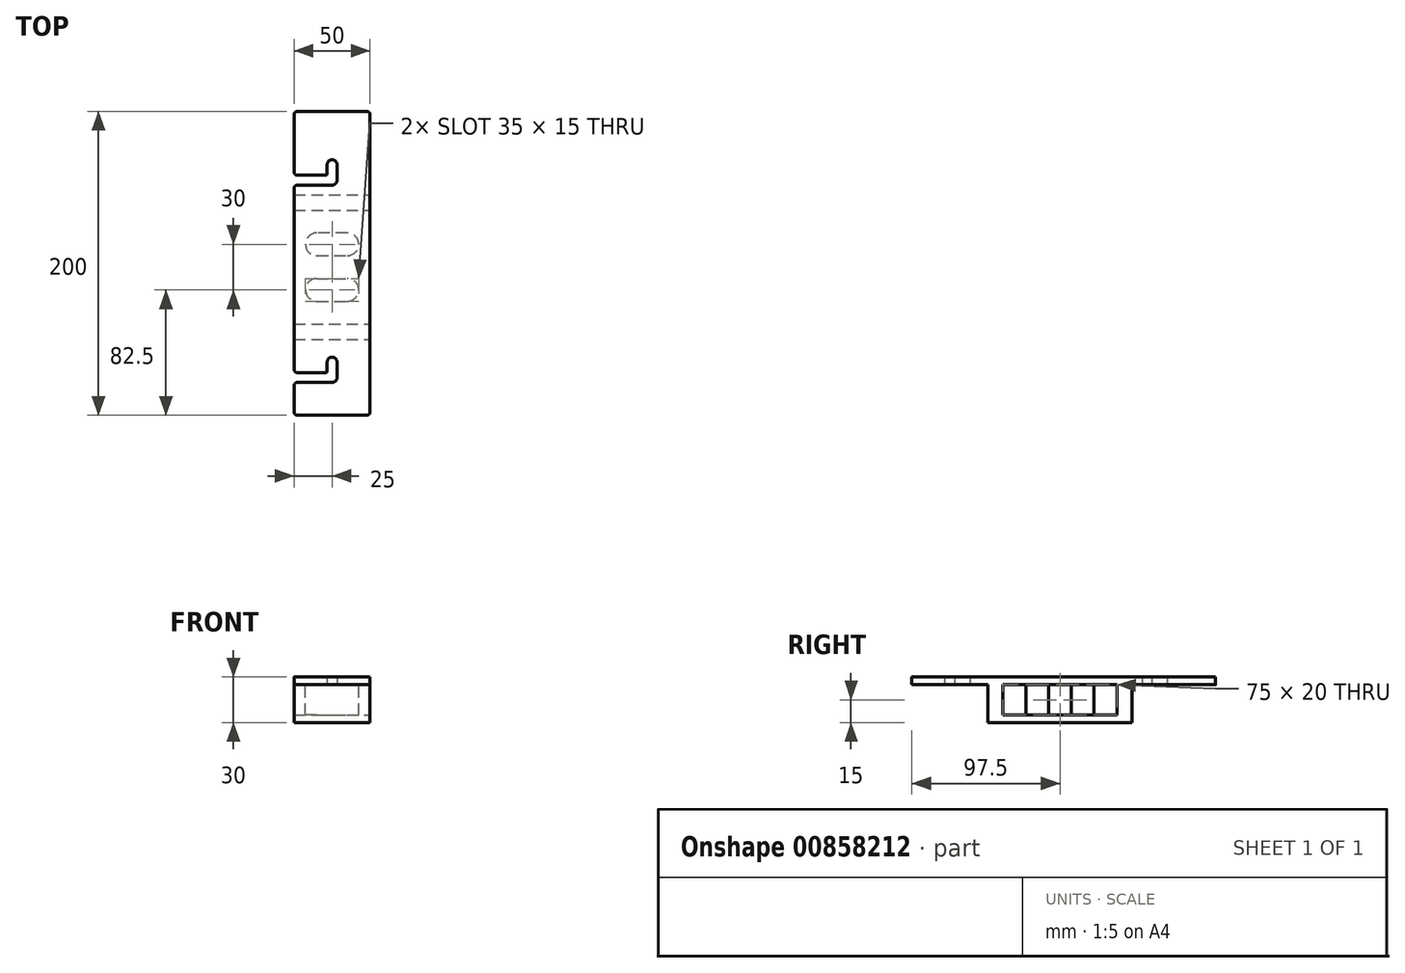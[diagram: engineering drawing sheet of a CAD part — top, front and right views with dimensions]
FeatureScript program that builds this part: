
annotation { "Feature Type Name" : "Feature", "Feature Type Description" : "" }
export const myFeature = defineFeature(function(context is Context, id is Id, definition is map)
    precondition{}
    {
        {
            var Q0;
            Q0=qCreatedBy(makeId("Top.planeOp"),FACE);
            var sketch = newSketch(context, id + "F0", { "sketchPlane" : qUnion([Q0])});
            skLineSegment(sketch, "E0.bottom", {"start": v(23, -100) * mm, "end": v(-23, -100) * mm});
            skLineSegment(sketch, "E0.top", {"start": v(23, 100) * mm, "end": v(-23, 100) * mm});
            skLineSegment(sketch, "E0.left", {"start": v(25, -98) * mm, "end": v(25, 98) * mm});
            skLineSegment(sketch, "E0.right", {"start": v(-25, -98) * mm, "end": v(-25, -80.5) * mm});
            skPoint(sketch, "E0.middle", {"position": v(0, 0) * mm});
            skLineSegment(sketch, "E1", {"start": v(-3.25, 65) * mm, "end": v(-3.25, 59) * mm});
            skLineSegment(sketch, "E2", {"start": v(-4.25, 58) * mm, "end": v(-23, 58) * mm});
            skLineSegment(sketch, "E3", {"start": v(-23, 51.5) * mm, "end": v(0, 51.5) * mm});
            skLineSegment(sketch, "E4", {"start": v(3.25, 54.75) * mm, "end": v(3.25, 65) * mm});
            skArc(sketch, "E5", {"start": v(-3.25, 65) * mm, "mid": v(0, 68.25) * mm, "end": v(3.25, 65) * mm});
            skPoint(sketch, "E6.visualSharp", {"position": v(3.25, 51.5) * mm});
            skArc(sketch, "E6.filletArc", {"start": v(0, 51.5) * mm, "mid": v(2.3, 52.45) * mm, "end": v(3.25, 54.75) * mm});
            skPoint(sketch, "E7.visualSharp", {"position": v(-3.25, 58) * mm});
            skArc(sketch, "E7.filletArc", {"start": v(-4.25, 58) * mm, "mid": v(-3.54, 58.3) * mm, "end": v(-3.25, 59) * mm});
            skLineSegment(sketch, "E8.trimOffspring", {"start": v(-25, 60) * mm, "end": v(-25, 98) * mm});
            skPoint(sketch, "E9.visualSharp", {"position": v(-25, 58) * mm});
            skArc(sketch, "E9.filletArc", {"start": v(-25, 60) * mm, "mid": v(-24.41, 58.59) * mm, "end": v(-23, 58) * mm});
            skPoint(sketch, "E10.visualSharp", {"position": v(-25, 51.5) * mm});
            skArc(sketch, "E10.filletArc", {"start": v(-23, 51.5) * mm, "mid": v(-24.41, 50.91) * mm, "end": v(-25, 49.5) * mm});
            skLineSegment(sketch, "E11", {"start": v(-3.25, -65) * mm, "end": v(-3.25, -71) * mm});
            skLineSegment(sketch, "E12", {"start": v(-4.25, -72) * mm, "end": v(-23, -72) * mm});
            skLineSegment(sketch, "E13", {"start": v(-23, -78.5) * mm, "end": v(0, -78.5) * mm});
            skLineSegment(sketch, "E14", {"start": v(3.25, -75.25) * mm, "end": v(3.25, -65) * mm});
            skArc(sketch, "E15", {"start": v(-3.25, -65) * mm, "mid": v(0, -61.75) * mm, "end": v(3.25, -65) * mm});
            skPoint(sketch, "E16.visualSharp", {"position": v(3.25, -78.5) * mm});
            skArc(sketch, "E16.filletArc", {"start": v(0, -78.5) * mm, "mid": v(2.3, -77.55) * mm, "end": v(3.25, -75.25) * mm});
            skPoint(sketch, "E17.visualSharp", {"position": v(-3.25, -72) * mm});
            skArc(sketch, "E17.filletArc", {"start": v(-4.25, -72) * mm, "mid": v(-3.54, -71.7) * mm, "end": v(-3.25, -71) * mm});
            skPoint(sketch, "E18.visualSharp", {"position": v(-24.01, -72) * mm});
            skArc(sketch, "E18.filletArc", {"start": v(-25, -70) * mm, "mid": v(-24.41, -71.41) * mm, "end": v(-23, -72) * mm});
            skPoint(sketch, "E19.visualSharp", {"position": v(-24.01, -78.5) * mm});
            skArc(sketch, "E19.filletArc", {"start": v(-23, -78.5) * mm, "mid": v(-24.41, -79.09) * mm, "end": v(-25, -80.5) * mm});
            skLineSegment(sketch, "E20.trimOffspring", {"start": v(-25, -70) * mm, "end": v(-25, 49.5) * mm});
            skPoint(sketch, "E21.visualSharp", {"position": v(-25, 100) * mm});
            skArc(sketch, "E21.filletArc", {"start": v(-23, 100) * mm, "mid": v(-24.41, 99.41) * mm, "end": v(-25, 98) * mm});
            skPoint(sketch, "E22.visualSharp", {"position": v(25, 100) * mm});
            skArc(sketch, "E22.filletArc", {"start": v(25, 98) * mm, "mid": v(24.41, 99.41) * mm, "end": v(23, 100) * mm});
            skPoint(sketch, "E23.visualSharp", {"position": v(25, -100) * mm});
            skArc(sketch, "E23.filletArc", {"start": v(23, -100) * mm, "mid": v(24.41, -99.41) * mm, "end": v(25, -98) * mm});
            skPoint(sketch, "E24.visualSharp", {"position": v(-25, -100) * mm});
            skArc(sketch, "E24.filletArc", {"start": v(-25, -98) * mm, "mid": v(-24.41, -99.41) * mm, "end": v(-23, -100) * mm});
            skSolve(sketch);
        }
        {
            var Q0;
            Q0 = qSketchRegion(id + "F0", true);
            extrude(context, id + "F1", {"entities" : qUnion([Q0]), "depth" : 5 * mm, "offsetDistance" : 25 * mm});
        }
        {
            var Q0;
            Q0=makeQuery(id+"F1.opExtrude","CAP_FACE",FACE,{"disambiguationData":[OSD([sQuery(id+"F0.wireOp",EDGE,"E0.bottom"),sQuery(id+"F0.wireOp",EDGE,"E0.top"),sQuery(id+"F0.wireOp",EDGE,"E0.left"),sQuery(id+"F0.wireOp",EDGE,"E0.right"),sQuery(id+"F0.wireOp",EDGE,"E1"),sQuery(id+"F0.wireOp",EDGE,"E2"),sQuery(id+"F0.wireOp",EDGE,"E3"),sQuery(id+"F0.wireOp",EDGE,"E4"),sQuery(id+"F0.wireOp",EDGE,"E5"),sQuery(id+"F0.wireOp",EDGE,"E6.filletArc"),sQuery(id+"F0.wireOp",EDGE,"E7.filletArc"),sQuery(id+"F0.wireOp",EDGE,"E8.trimOffspring"),sQuery(id+"F0.wireOp",EDGE,"E9.filletArc"),sQuery(id+"F0.wireOp",EDGE,"E10.filletArc"),sQuery(id+"F0.wireOp",EDGE,"E11"),sQuery(id+"F0.wireOp",EDGE,"E12"),sQuery(id+"F0.wireOp",EDGE,"E13"),sQuery(id+"F0.wireOp",EDGE,"E14"),sQuery(id+"F0.wireOp",EDGE,"E15"),sQuery(id+"F0.wireOp",EDGE,"E16.filletArc"),sQuery(id+"F0.wireOp",EDGE,"E17.filletArc"),sQuery(id+"F0.wireOp",EDGE,"E18.filletArc"),sQuery(id+"F0.wireOp",EDGE,"E19.filletArc"),sQuery(id+"F0.wireOp",EDGE,"E20.trimOffspring"),sQuery(id+"F0.wireOp",EDGE,"E21.filletArc"),sQuery(id+"F0.wireOp",EDGE,"E22.filletArc"),sQuery(id+"F0.wireOp",EDGE,"E23.filletArc"),sQuery(id+"F0.wireOp",EDGE,"E24.filletArc")])],"isStart":true});
            var sketch = newSketch(context, id + "F2", { "sketchPlane" : qUnion([Q0])});
            skArc(sketch, "E25", {"start": v(-10, 25) * mm, "mid": v(-17.5, 17.5) * mm, "end": v(-10, 10) * mm});
            skArc(sketch, "E26", {"start": v(10, 10) * mm, "mid": v(17.5, 17.5) * mm, "end": v(10, 25) * mm});
            skLineSegment(sketch, "E27", {"start": v(-10, 25) * mm, "end": v(10, 25) * mm});
            skLineSegment(sketch, "E28", {"start": v(-10, 10) * mm, "end": v(10, 10) * mm});
            skLineSegment(sketch, "E29", {"start": v(-10, -5) * mm, "end": v(10, -5) * mm});
            skArc(sketch, "E30", {"start": v(10, -5) * mm, "mid": v(17.5, -12.5) * mm, "end": v(10, -20) * mm});
            skLineSegment(sketch, "E31", {"start": v(10, -20) * mm, "end": v(-10, -20) * mm});
            skArc(sketch, "E32", {"start": v(-10, -20) * mm, "mid": v(-17.5, -12.5) * mm, "end": v(-10, -5) * mm});
            skLineSegment(sketch, "E33.bottom", {"start": v(-25, 50) * mm, "end": v(25, 50) * mm});
            skLineSegment(sketch, "E33.top", {"start": v(-25, 40) * mm, "end": v(25, 40) * mm});
            skLineSegment(sketch, "E33.left", {"start": v(-25, 50) * mm, "end": v(-25, 40) * mm});
            skLineSegment(sketch, "E33.right", {"start": v(25, 50) * mm, "end": v(25, 40) * mm});
            skLineSegment(sketch, "E34.bottom", {"start": v(-25, -35) * mm, "end": v(25, -35) * mm});
            skLineSegment(sketch, "E34.top", {"start": v(-25, -45) * mm, "end": v(25, -45) * mm});
            skLineSegment(sketch, "E34.left", {"start": v(-25, -35) * mm, "end": v(-25, -45) * mm});
            skLineSegment(sketch, "E34.right", {"start": v(25, -35) * mm, "end": v(25, -45) * mm});
            skSolve(sketch);
        }
        {
            var Q0;
            Q0 = qSketchRegion(id + "F2", true);
            extrude(context, id + "F3", {"entities" : qUnion([Q0]), "operationType" : NewBodyOperationType.ADD, "depth" : 20 * mm, "offsetDistance" : 25 * mm});
        }
        {
            var Q0;
            Q0=makeQuery(id+"F3.opExtrude","CAP_FACE",FACE,{"disambiguationData":[OSD([sQuery(id+"F2.wireOp",EDGE,"E33.bottom"),sQuery(id+"F2.wireOp",EDGE,"E33.top"),sQuery(id+"F2.wireOp",EDGE,"E33.left"),sQuery(id+"F2.wireOp",EDGE,"E33.right")])],"isStart":false});
            var sketch = newSketch(context, id + "F4", { "sketchPlane" : qUnion([Q0])});
            skLineSegment(sketch, "E35.bottom", {"start": v(-25, 50) * mm, "end": v(25, 50) * mm});
            skLineSegment(sketch, "E35.top", {"start": v(-25, -45) * mm, "end": v(25, -45) * mm});
            skLineSegment(sketch, "E35.left", {"start": v(-25, 50) * mm, "end": v(-25, -45) * mm});
            skLineSegment(sketch, "E35.right", {"start": v(25, 50) * mm, "end": v(25, -45) * mm});
            skSolve(sketch);
        }
        {
            var Q0;
            Q0 = qSketchRegion(id + "F4", true);
            extrude(context, id + "F5", {"entities" : qUnion([Q0]), "operationType" : NewBodyOperationType.ADD, "depth" : 5 * mm, "offsetDistance" : 25 * mm});
        }
    });
